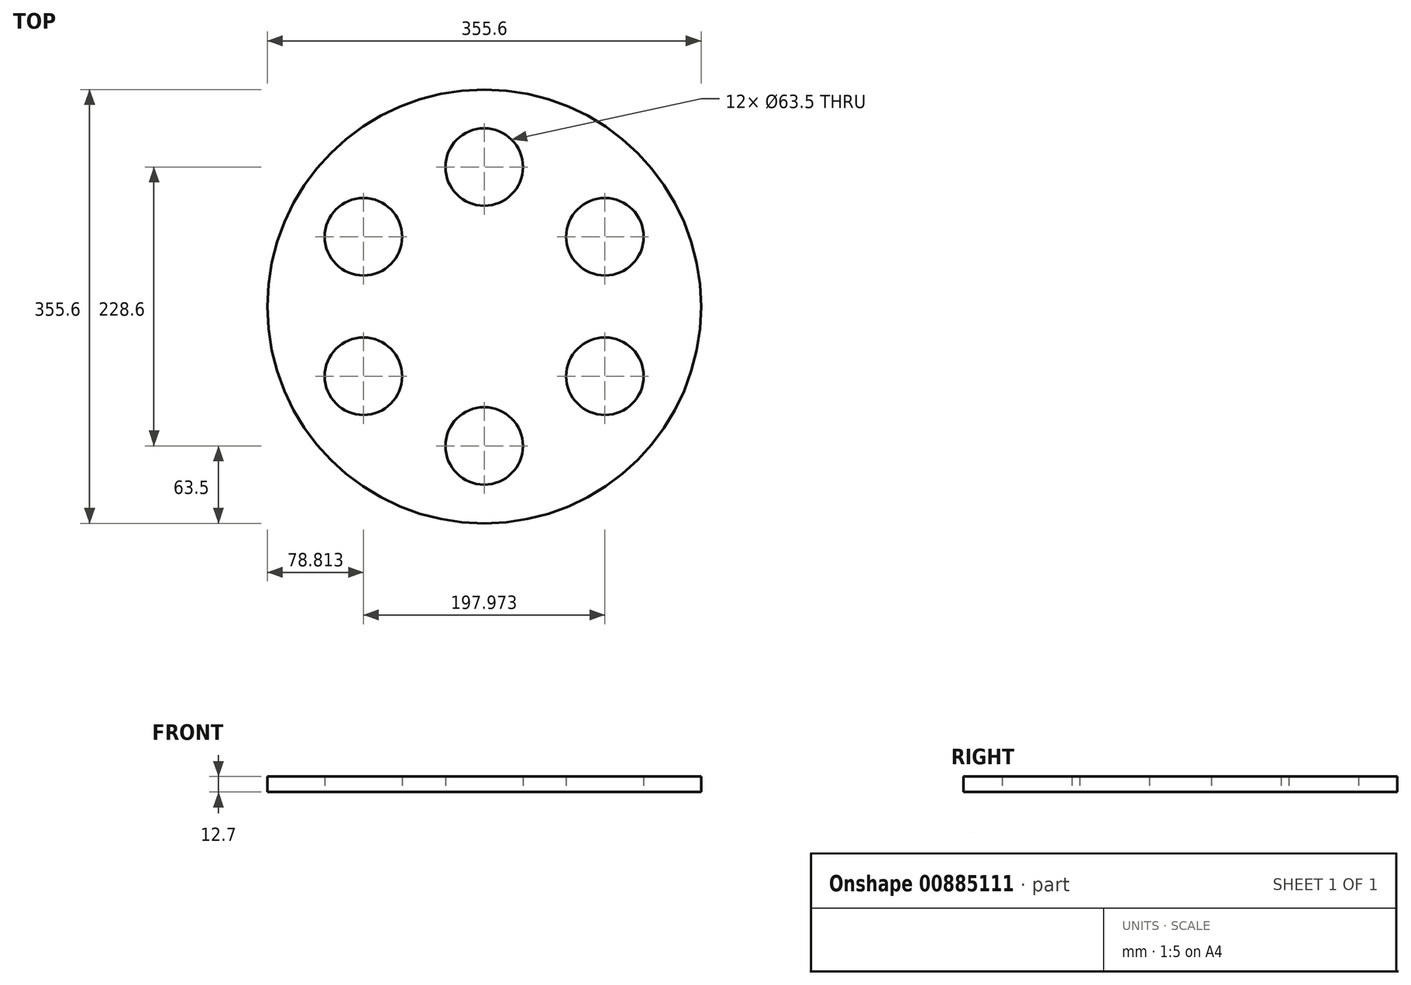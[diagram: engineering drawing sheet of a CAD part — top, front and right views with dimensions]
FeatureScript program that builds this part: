
annotation { "Feature Type Name" : "Feature", "Feature Type Description" : "" }
export const myFeature = defineFeature(function(context is Context, id is Id, definition is map)
    precondition{}
    {
        {
            var Q0;
            Q0=qCreatedBy(makeId("Top.planeOp"),FACE);
            var sketch = newSketch(context, id + "F0", { "sketchPlane" : qUnion([Q0])});
            skCircle(sketch, "E0", {"center": v(0, 0) * mm, "radius": 165.1 * mm, "construction": true});
            skCircle(sketch, "E1", {"center": v(0, 114.3) * mm, "radius": 50.8 * mm, "construction": true});
            skLineSegment(sketch, "E2", {"start": v(0, 114.3) * mm, "end": v(0, 0) * mm, "construction": true});
            skCircle(sketch, "E3", {"center": v(0, 114.3) * mm, "radius": 31.75 * mm});
            skCircle(sketch, "E4.1.0", {"center": v(-98.99, 57.15) * mm, "radius": 31.75 * mm});
            skCircle(sketch, "E4.1.1", {"center": v(-98.99, 57.15) * mm, "radius": 50.8 * mm, "construction": true});
            skCircle(sketch, "E4.2.0", {"center": v(-98.99, -57.15) * mm, "radius": 31.75 * mm});
            skCircle(sketch, "E4.2.1", {"center": v(-98.99, -57.15) * mm, "radius": 50.8 * mm, "construction": true});
            skCircle(sketch, "E4.3.0", {"center": v(0, -114.3) * mm, "radius": 31.75 * mm});
            skCircle(sketch, "E4.3.1", {"center": v(0, -114.3) * mm, "radius": 50.8 * mm, "construction": true});
            skCircle(sketch, "E4.4.0", {"center": v(98.99, -57.15) * mm, "radius": 31.75 * mm});
            skCircle(sketch, "E4.4.1", {"center": v(98.99, -57.15) * mm, "radius": 50.8 * mm, "construction": true});
            skCircle(sketch, "E4.5.0", {"center": v(98.99, 57.15) * mm, "radius": 31.75 * mm});
            skCircle(sketch, "E4.5.1", {"center": v(98.99, 57.15) * mm, "radius": 50.8 * mm, "construction": true});
            skCircle(sketch, "E5", {"center": v(0, 0) * mm, "radius": 177.8 * mm});
            skSolve(sketch);
        }
        {
            var Q0;
            Q0 = qSketchRegion(id + "F0", true);
            extrude(context, id + "F1", {"entities" : qUnion([Q0]), "depth" : 12.7 * mm, "offsetDistance" : 25.4 * mm});
        }
    });
